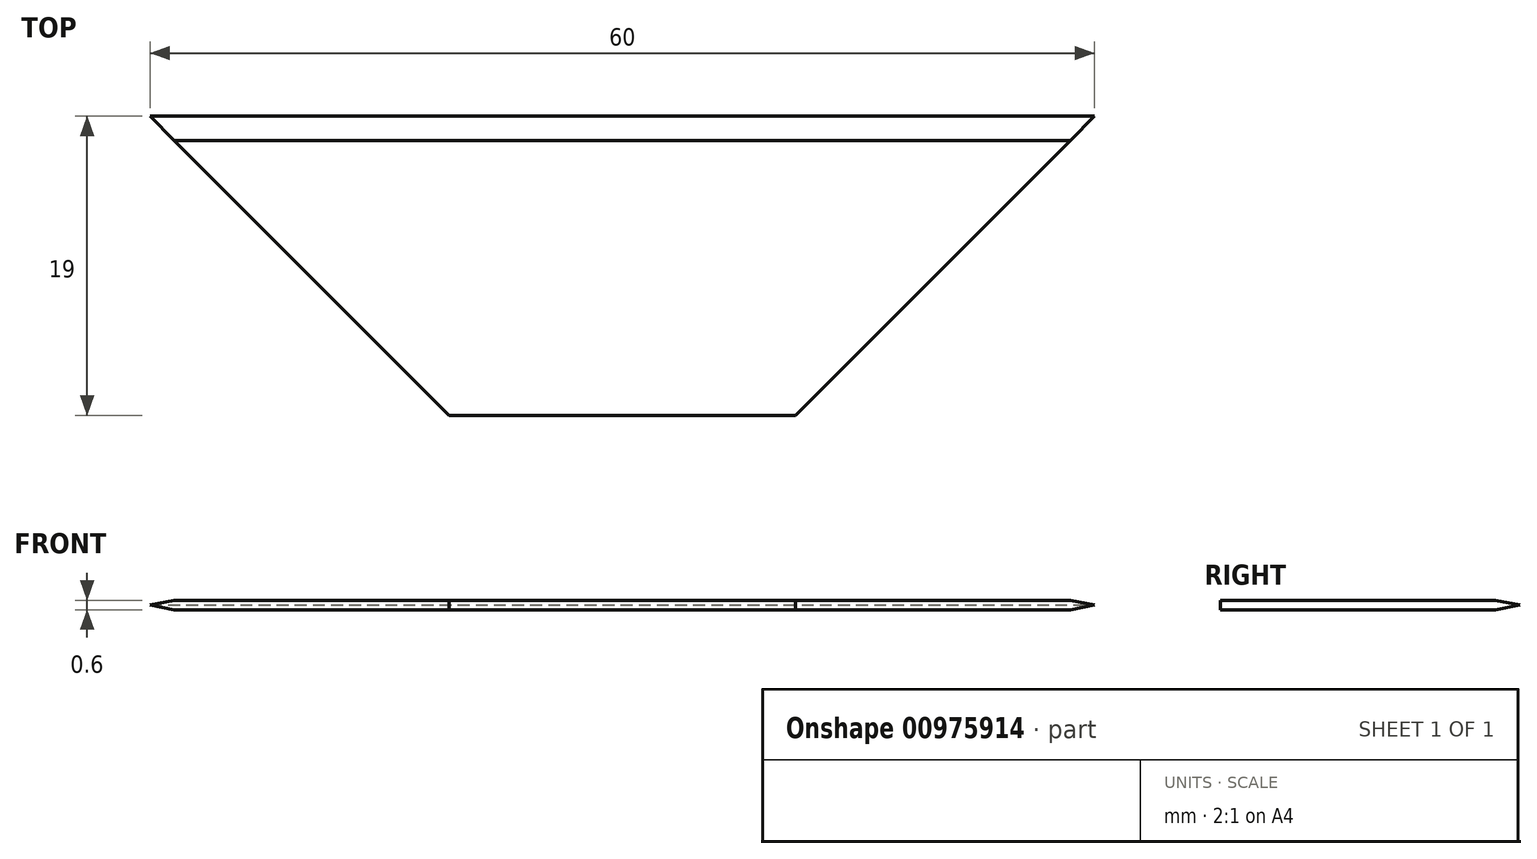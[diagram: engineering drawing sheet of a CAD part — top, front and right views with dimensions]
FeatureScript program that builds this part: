
annotation { "Feature Type Name" : "Feature", "Feature Type Description" : "" }
export const myFeature = defineFeature(function(context is Context, id is Id, definition is map)
    precondition{}
    {
        {
            var Q0;
            Q0=qCreatedBy(makeId("Top.planeOp"),FACE);
            var sketch = newSketch(context, id + "F0", { "sketchPlane" : qUnion([Q0])});
            skLineSegment(sketch, "E0.bottom", {"start": v(-30, 9.5) * mm, "end": v(30, 9.5) * mm});
            skPoint(sketch, "E0.middle", {"position": v(0, 0) * mm});
            skLineSegment(sketch, "E1", {"start": v(-30, 9.5) * mm, "end": v(-11, -9.5) * mm});
            skLineSegment(sketch, "E2", {"start": v(30, 9.5) * mm, "end": v(11, -9.5) * mm});
            skLineSegment(sketch, "E3", {"start": v(-11, -9.5) * mm, "end": v(11, -9.5) * mm});
            skSolve(sketch);
        }
        {
            var Q0;
            Q0=makeQuery(id+"F0.imprint","IMPRINT",FACE,{"disambiguationData":[TD([[makeQuery(id+"F0.imprint","IMPRINT",EDGE,{"derivedFrom":sQuery(id+"F0.wireOp",EDGE,"E0.bottom")}),-1.0]])]});
            extrude(context, id + "F1", {"entities" : qUnion([Q0]), "endBound" : BoundingType.SYMMETRIC, "depth" : 0.6 * mm, "offsetDistance" : 25 * mm});
        }
        {
            var Q0;
            Q0=qCreatedBy(makeId("Right.planeOp"),FACE);
            var sketch = newSketch(context, id + "F2", { "sketchPlane" : qUnion([Q0])});
            skPoint(sketch, "E4.0", {"position": v(9.5, 0) * mm});
            skPoint(sketch, "E5.0", {"position": v(0, 0) * mm});
            skLineSegment(sketch, "E6.0", {"start": v(9.5, 0.3) * mm, "end": v(-9.5, 0.3) * mm});
            skLineSegment(sketch, "E6.1", {"start": v(9.5, -0.3) * mm, "end": v(-9.5, -0.3) * mm});
            skLineSegment(sketch, "E6.2", {"start": v(9.5, 0.3) * mm, "end": v(9.5, -0.3) * mm});
            skLineSegment(sketch, "E7", {"start": v(9.5, 0) * mm, "end": v(7.96, 0.3) * mm});
            skLineSegment(sketch, "E8", {"start": v(9.5, 0) * mm, "end": v(7.96, -0.3) * mm});
            skSolve(sketch);
        }
        {
            var Q0;
            {var subQ3=sQuery(id+"F2.wireOp",EDGE,"E7");Q0=makeQuery(id+"F2.imprint","IMPRINT",FACE,{"disambiguationData":[TD([[makeQuery(id+"F2.imprint","IMPRINT",EDGE,{"derivedFrom":subQ3}),-1.0]])]});}
            var Q1;
            {var subQ3=sQuery(id+"F2.wireOp",EDGE,"E8");Q1=makeQuery(id+"F2.imprint","IMPRINT",FACE,{"disambiguationData":[TD([[makeQuery(id+"F2.imprint","IMPRINT",EDGE,{"derivedFrom":subQ3}),1.0]])]});}
            extrude(context, id + "F3", {"entities" : qUnion([Q0, Q1]), "operationType" : NewBodyOperationType.REMOVE, "endBound" : BoundingType.SYMMETRIC, "oppositeDirection" : true, "depth" : 60 * mm, "offsetDistance" : 25 * mm});
        }
    });
